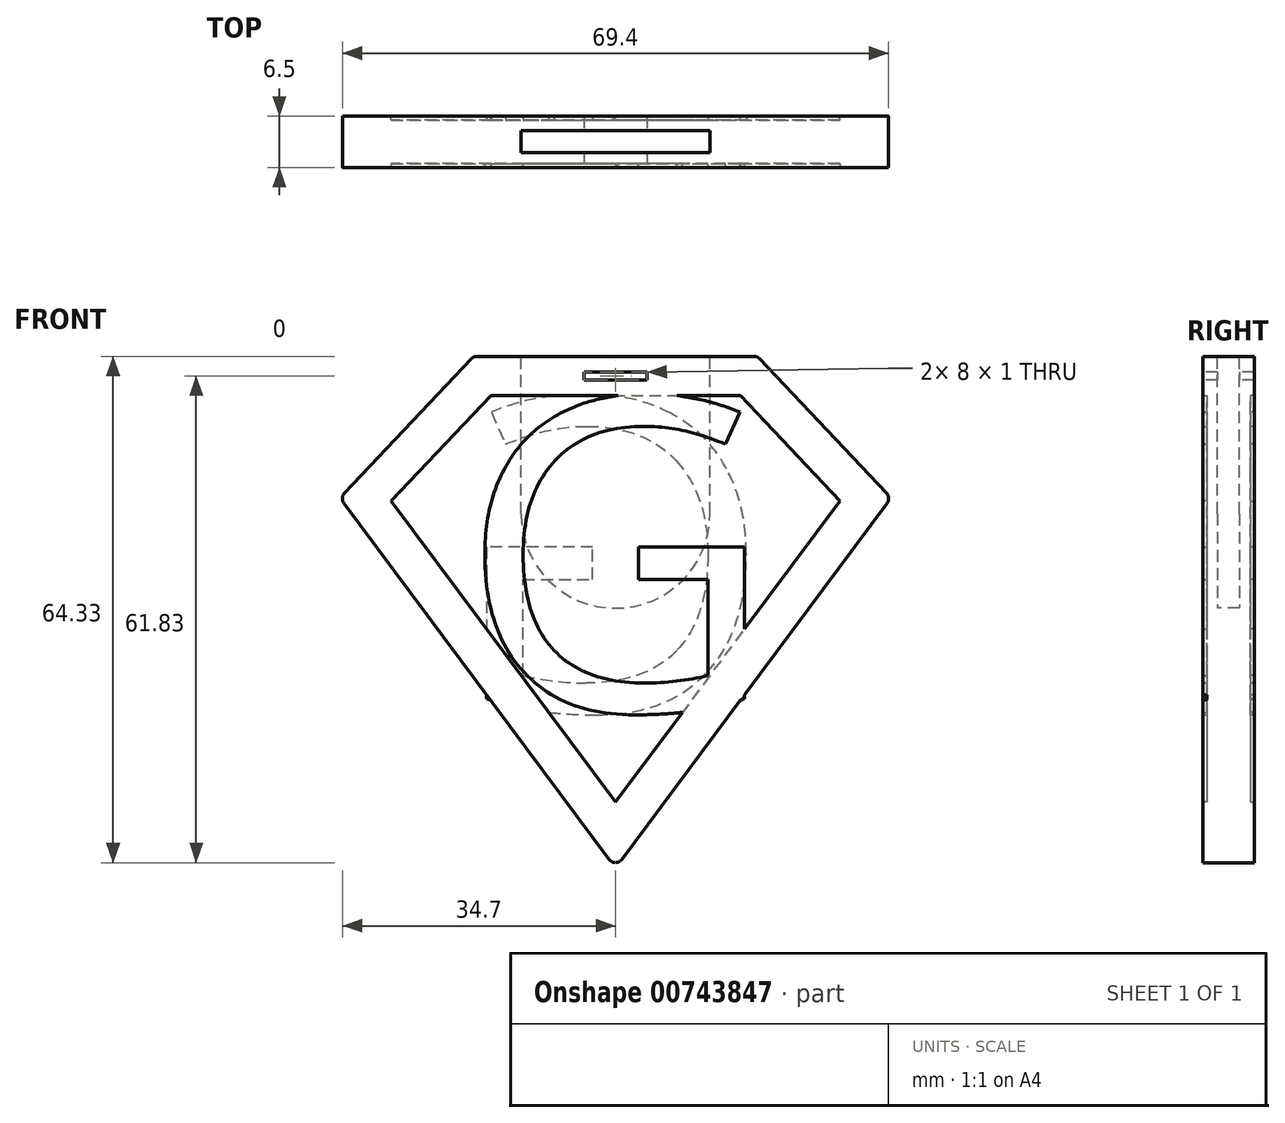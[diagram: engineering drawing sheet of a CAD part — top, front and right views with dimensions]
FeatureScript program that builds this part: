
annotation { "Feature Type Name" : "Feature", "Feature Type Description" : "" }
export const myFeature = defineFeature(function(context is Context, id is Id, definition is map)
    precondition{}
    {
        {
            var Q0;
            Q0=qCreatedBy(makeId("Front.planeOp"),FACE);
            var sketch = newSketch(context, id + "F0", { "sketchPlane" : qUnion([Q0])});
            skLineSegment(sketch, "E0", {"start": v(0, 18) * mm, "end": v(18, 18) * mm});
            skLineSegment(sketch, "E1", {"start": v(18, 18) * mm, "end": v(35, 0) * mm});
            skLineSegment(sketch, "E2", {"start": v(35, 0) * mm, "end": v(0, -47) * mm});
            skLineSegment(sketch, "E3", {"start": v(0, 18) * mm, "end": v(0, -47) * mm, "construction": true});
            skLineSegment(sketch, "E4.MirrorCS", {"start": v(-35, 0) * mm, "end": v(0, -47) * mm});
            skLineSegment(sketch, "E5.MirrorCS", {"start": v(-18, 18) * mm, "end": v(-35, 0) * mm});
            skLineSegment(sketch, "E6.MirrorCS", {"start": v(0, 18) * mm, "end": v(-18, 18) * mm});
            skSolve(sketch);
        }
        {
            var Q0;
            Q0=qSketchRegion(id+"F0",true);
            extrude(context, id + "F1", {"entities" : qUnion([Q0]), "endBound" : BoundingType.SYMMETRIC, "depth" : 6.5 * mm, "offsetDistance" : 25 * mm});
        }
        {
            var Q0;
            Q0=makeQuery(id+"F1.opExtrude","CAP_FACE",FACE,{"disambiguationData":[OSD([sQuery(id+"F0.wireOp",EDGE,"E0"),sQuery(id+"F0.wireOp",EDGE,"E1"),sQuery(id+"F0.wireOp",EDGE,"E2"),sQuery(id+"F0.wireOp",EDGE,"E4.MirrorCS"),sQuery(id+"F0.wireOp",EDGE,"E5.MirrorCS"),sQuery(id+"F0.wireOp",EDGE,"E6.MirrorCS")])],"isStart":false});
            var sketch = newSketch(context, id + "F2", { "sketchPlane" : qUnion([Q0])});
            skLineSegment(sketch, "E7.0", {"start": v(-15.84, 13) * mm, "end": v(15.84, 13) * mm});
            skLineSegment(sketch, "E8.0", {"start": v(-15.84, 13) * mm, "end": v(-28.48, -0.38) * mm});
            skLineSegment(sketch, "E9.0", {"start": v(-28.48, -0.38) * mm, "end": v(0, -38.63) * mm});
            skLineSegment(sketch, "E10.0", {"start": v(28.48, -0.38) * mm, "end": v(0, -38.63) * mm});
            skLineSegment(sketch, "E11.0", {"start": v(15.84, 13) * mm, "end": v(28.48, -0.38) * mm});
            skSolve(sketch);
        }
        {
            var Q0;
            Q0=qSketchRegion(id+"F2",true);
            extrude(context, id + "F3", {"entities" : qUnion([Q0]), "operationType" : NewBodyOperationType.REMOVE, "oppositeDirection" : true, "depth" : 0.5 * mm, "offsetDistance" : 25 * mm});
        }
        {
            var Q0;
            Q0=makeQuery(id+"F1.opExtrude","CAP_FACE",FACE,{"disambiguationData":[OSD([sQuery(id+"F0.wireOp",EDGE,"E0"),sQuery(id+"F0.wireOp",EDGE,"E1"),sQuery(id+"F0.wireOp",EDGE,"E2"),sQuery(id+"F0.wireOp",EDGE,"E4.MirrorCS"),sQuery(id+"F0.wireOp",EDGE,"E5.MirrorCS"),sQuery(id+"F0.wireOp",EDGE,"E6.MirrorCS")])],"isStart":true});
            var sketch = newSketch(context, id + "F4", { "sketchPlane" : qUnion([Q0])});
            skLineSegment(sketch, "E12.0", {"start": v(15.84, 13) * mm, "end": v(-15.84, 13) * mm});
            skLineSegment(sketch, "E13.0", {"start": v(15.84, 13) * mm, "end": v(28.48, -0.38) * mm});
            skLineSegment(sketch, "E14.0", {"start": v(28.48, -0.38) * mm, "end": v(0, -38.63) * mm});
            skLineSegment(sketch, "E15.0", {"start": v(-28.48, -0.38) * mm, "end": v(0, -38.63) * mm});
            skLineSegment(sketch, "E15.1", {"start": v(-15.84, 13) * mm, "end": v(-28.48, -0.38) * mm});
            skSolve(sketch);
        }
        {
            var Q0;
            Q0=qSketchRegion(id+"F4",true);
            extrude(context, id + "F5", {"entities" : qUnion([Q0]), "operationType" : NewBodyOperationType.REMOVE, "oppositeDirection" : true, "depth" : 0.5 * mm, "offsetDistance" : 25 * mm});
        }
        {
            var Q0;
            Q0=makeQuery(id+"F3.boolean.opBoolean","COPY",FACE,{"derivedFrom":makeQuery(id+"F3.opExtrude","CAP_FACE",FACE,{"disambiguationData":[OSD([sQuery(id+"F2.wireOp",EDGE,"E7.0"),sQuery(id+"F2.wireOp",EDGE,"E8.0"),sQuery(id+"F2.wireOp",EDGE,"E9.0"),sQuery(id+"F2.wireOp",EDGE,"E10.0"),sQuery(id+"F2.wireOp",EDGE,"E11.0")])],"isStart":false})});
            var sketch = newSketch(context, id + "F6", { "sketchPlane" : qUnion([Q0])});
            skText(sketch, "E16", { "text": "G", "fontName": "OpenSans-Regular.ttf"});
            const initialGuessF6  = {"E16": [-0.02, -0.027, 1, 0, 0.04]};
            skSetInitialGuess(sketch, initialGuessF6);
            skSolve(sketch);
        }
        {
            var Q0;
            Q0=qSketchRegion(id+"F6",true);
            extrude(context, id + "F7", {"entities" : qUnion([Q0]), "operationType" : NewBodyOperationType.ADD, "depth" : 0.5 * mm, "offsetDistance" : 25 * mm});
        }
        {
            var Q0;
            Q0=makeQuery(id+"F5.boolean.opBoolean","COPY",FACE,{"derivedFrom":makeQuery(id+"F5.opExtrude","CAP_FACE",FACE,{"disambiguationData":[OSD([sQuery(id+"F4.wireOp",EDGE,"E12.0"),sQuery(id+"F4.wireOp",EDGE,"E13.0"),sQuery(id+"F4.wireOp",EDGE,"E14.0"),sQuery(id+"F4.wireOp",EDGE,"E15.0"),sQuery(id+"F4.wireOp",EDGE,"E15.1")])],"isStart":false})});
            var sketch = newSketch(context, id + "F8", { "sketchPlane" : qUnion([Q0])});
            skText(sketch, "E17", { "text": "G", "fontName": "OpenSans-Regular.ttf"});
            const initialGuessF8  = {"E17": [-0.02, -0.027, 1, 0, 0.04]};
            skSetInitialGuess(sketch, initialGuessF8);
            skSolve(sketch);
        }
        {
            var Q0;
            Q0=qSketchRegion(id+"F8",true);
            extrude(context, id + "F9", {"entities" : qUnion([Q0]), "operationType" : NewBodyOperationType.ADD, "depth" : 0.5 * mm, "offsetDistance" : 25 * mm});
        }
        {
            var Q0;
            Q0=makeQuery(id+"F1.opExtrude","SWEPT_FACE",FACE,{"disambiguationData":[OSD([sQuery(id+"F0.wireOp",EDGE,"E0"),sQuery(id+"F0.wireOp",EDGE,"E6.MirrorCS")])]});
            var sketch = newSketch(context, id + "F10", { "sketchPlane" : qUnion([Q0])});
            skLineSegment(sketch, "E18.bottom", {"start": v(-12, 1.4) * mm, "end": v(12, 1.4) * mm});
            skLineSegment(sketch, "E18.top", {"start": v(-12, -1.4) * mm, "end": v(12, -1.4) * mm});
            skLineSegment(sketch, "E18.left", {"start": v(-12, 1.4) * mm, "end": v(-12, -1.4) * mm});
            skLineSegment(sketch, "E18.right", {"start": v(12, 1.4) * mm, "end": v(12, -1.4) * mm});
            skSolve(sketch);
        }
        {
            var Q0;
            Q0=qSketchRegion(id+"F10",true);
            extrude(context, id + "F11", {"entities" : qUnion([Q0]), "operationType" : NewBodyOperationType.REMOVE, "oppositeDirection" : true, "depth" : 20 * mm, "offsetDistance" : 25 * mm});
        }
        {
            var Q0;
            Q0=qCreatedBy(makeId("Front.planeOp"),FACE);
            var sketch = newSketch(context, id + "F12", { "sketchPlane" : qUnion([Q0])});
            skLineSegment(sketch, "E19.0", {"start": v(-12, -2) * mm, "end": v(12, -2) * mm});
            skArc(sketch, "E20", {"start": v(-12, -2) * mm, "mid": v(0, -14) * mm, "end": v(12, -2) * mm});
            skSolve(sketch);
        }
        {
            var Q0;
            Q0=qSketchRegion(id+"F12",true);
            extrude(context, id + "F13", {"entities" : qUnion([Q0]), "operationType" : NewBodyOperationType.REMOVE, "endBound" : BoundingType.SYMMETRIC, "oppositeDirection" : true, "depth" : 2.8 * mm, "offsetDistance" : 25 * mm});
        }
        {
            var Q0;
            Q0=makeQuery(id+"F1.opExtrude","CAP_FACE",FACE,{"disambiguationData":[OSD([sQuery(id+"F0.wireOp",EDGE,"E0"),sQuery(id+"F0.wireOp",EDGE,"E1"),sQuery(id+"F0.wireOp",EDGE,"E2"),sQuery(id+"F0.wireOp",EDGE,"E4.MirrorCS"),sQuery(id+"F0.wireOp",EDGE,"E5.MirrorCS"),sQuery(id+"F0.wireOp",EDGE,"E6.MirrorCS")])],"isStart":false});
            var sketch = newSketch(context, id + "F14", { "sketchPlane" : qUnion([Q0])});
            skLineSegment(sketch, "E21.bottom", {"start": v(-4, 16) * mm, "end": v(4, 16) * mm});
            skLineSegment(sketch, "E21.top", {"start": v(-4, 15) * mm, "end": v(4, 15) * mm});
            skLineSegment(sketch, "E21.left", {"start": v(-4, 16) * mm, "end": v(-4, 15) * mm});
            skLineSegment(sketch, "E21.right", {"start": v(4, 16) * mm, "end": v(4, 15) * mm});
            skSolve(sketch);
        }
        {
            var Q0;
            Q0=qSketchRegion(id+"F14",true);
            extrude(context, id + "F15", {"entities" : qUnion([Q0]), "operationType" : NewBodyOperationType.REMOVE, "oppositeDirection" : true, "depth" : 25 * mm, "offsetDistance" : 25 * mm});
        }
        {
            var Q0;
            Q0=makeQuery(id+"F1.opExtrude","SWEPT_EDGE",EDGE,{"disambiguationData":[OSD([sQuery(id+"F0.wireOp",EDGE,"E2"),sQuery(id+"F0.wireOp",EDGE,"E4.MirrorCS")])]});
            var Q1;
            Q1=makeQuery(id+"F1.opExtrude","SWEPT_EDGE",EDGE,{"disambiguationData":[OSD([sQuery(id+"F0.wireOp",EDGE,"E1"),sQuery(id+"F0.wireOp",EDGE,"E2")])]});
            var Q2;
            Q2=makeQuery(id+"F1.opExtrude","SWEPT_EDGE",EDGE,{"disambiguationData":[OSD([sQuery(id+"F0.wireOp",EDGE,"E4.MirrorCS"),sQuery(id+"F0.wireOp",EDGE,"E5.MirrorCS")])]});
            var Q3;
            Q3=makeQuery(id+"F1.opExtrude","SWEPT_EDGE",EDGE,{"disambiguationData":[OSD([sQuery(id+"F0.wireOp",EDGE,"E5.MirrorCS"),sQuery(id+"F0.wireOp",EDGE,"E6.MirrorCS")])]});
            var Q4;
            Q4=makeQuery(id+"F1.opExtrude","SWEPT_EDGE",EDGE,{"disambiguationData":[OSD([sQuery(id+"F0.wireOp",EDGE,"E0"),sQuery(id+"F0.wireOp",EDGE,"E1")])]});
            fillet(context, id + "F16", {"entities" : qUnion([Q0, Q1, Q2, Q3, Q4]), "radius" : 1 * mm, "tangentPropagation" : true, "allowEdgeOverflow" : false});
        }
    });
